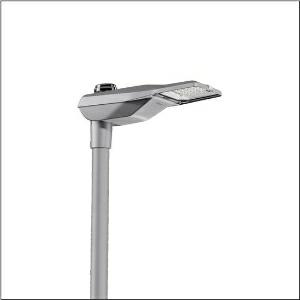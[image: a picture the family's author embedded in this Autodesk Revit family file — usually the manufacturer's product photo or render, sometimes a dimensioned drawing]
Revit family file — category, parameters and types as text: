
# Revit family: streetlight_sl_21_micro___st0_8a_5xe5c47n08db_8458
name_source: partatom
category: Lighting Fixtures
units: mm (PartAtom-declared; Revit-internal decimal feet)

## family parameters
Cut with Voids When Loaded = No
Host = Face
Light Source = No
Part Type = Normal
Room Calculation Point = No
Round Connector Dimension = Use Diameter
Shared = No

## types (1)
- --- (1 x LED, 5320 lm, 39.1 W, 4000K)
    Apparent Load = 39 VA
    CIE Flux Codes = 38 75 97 100 100
    Color Rendering = 70
    Color Temperature = 4000K
    Default Elevation = 1800 mm
    Description = Streetlight SL 21 micro, mast luminaire, primary light control with lens, of PMMA, primary optical cover: cover, of toughened safety glass, transparent, light distribution: ST0.8a, light emission: direct distribution, primary light characteristic: asymmetric, installation type: post-top, LED, 3G 1.5mm², High Power LED, rated luminous flux: 5.320lm, luminous efficacy: 136lm/W, light colour: 740, colour temperature: 4000K, control gear: NEMA (7pin), control: overheat protection, pre-setting: linear dimming characteristic, constant luminous flux control, time-dependent luminous flux control, flexible luminous flux parameterisation, mains connection: 230..240V, AC, 50/60Hz, connection cable pre-assembled, cable length: 6,5m, wiring characteristics: H07RN-F, start of lifetime: 39W, end of service life: 41W, reduction: 18W, luminaire housing, of diecast aluminium (EN AC-44300), powder-coated, Siteco® metallic grey (DB 702S), corrosivity category C5 mid according to DIN EN ISO 12944, multi-level sealing system, sealing non-destructively replaceable, inclination adjustable: 0°, 5°, 10°, 15°, length: 528mm, width: 235mm, height: 110mm, spigot size: 76/60mm (post-top), mounting height: 4..8m, protection rating (complete): IP66, insulation class (complete): insulation class I (protective earthing), certification: CE, ENEC, ENEC+, VDE, impact resistance: IK10, permissible operating ambient temperature for outdoor applications: -40..+50°C, standard-compliant lighting for roads and squares, packaging unit: 1 piece

Light Distribution: ST0.8a
    Height = 110 mm
    Lamp = 1 x LED
    Lamp Light Flux = 5320 lm
    Lamp Power = 39.1 W
    Lamp count = 1
    Length = 528 mm
    Luminous efficacy = 136 lm/W
    Manufacturer = Siteco
    ModVariant = No
    Model = 5XE5C47N08DB
    Number of Poles = 1
    OnlyDefault = Yes
    Power Factor = 1
    Product Name = Streetlight SL 21 micro | ST0.8a
    Product group = mast luminaire | pylon top
    ProductGroupID = 6100
    Protection Class = Protection class I
    Protection Degree = IP 66
    RLX_Detail_Level = 1
    RLX_Emergency_Light_Flux = 0 lm
    RLX_Emergency_Type = 0
    RLX_Emergency_Type_DB = No
    RlxData = <blob elided: 99329 chars, md5=0f9f6788>
    Socket = socket
    Standby Power = 0 W
    System Light Flux = 5320 lm
    System Power = 39 W
    Type Comments = factory setting: luminous flux: 100 % | dim-lin: 254 | 765 mA
    Type Image = l_1294375.jpg
    URL = http://relux.com
    VarID = @adj_134304
    Voltage = 0 V
    Weight = 0.00 kg
    Width = 235 mm

## geometry (parser evidence)
native form markers: Blend x4, Sweep x10
no freeform markers — native parametric forms only
